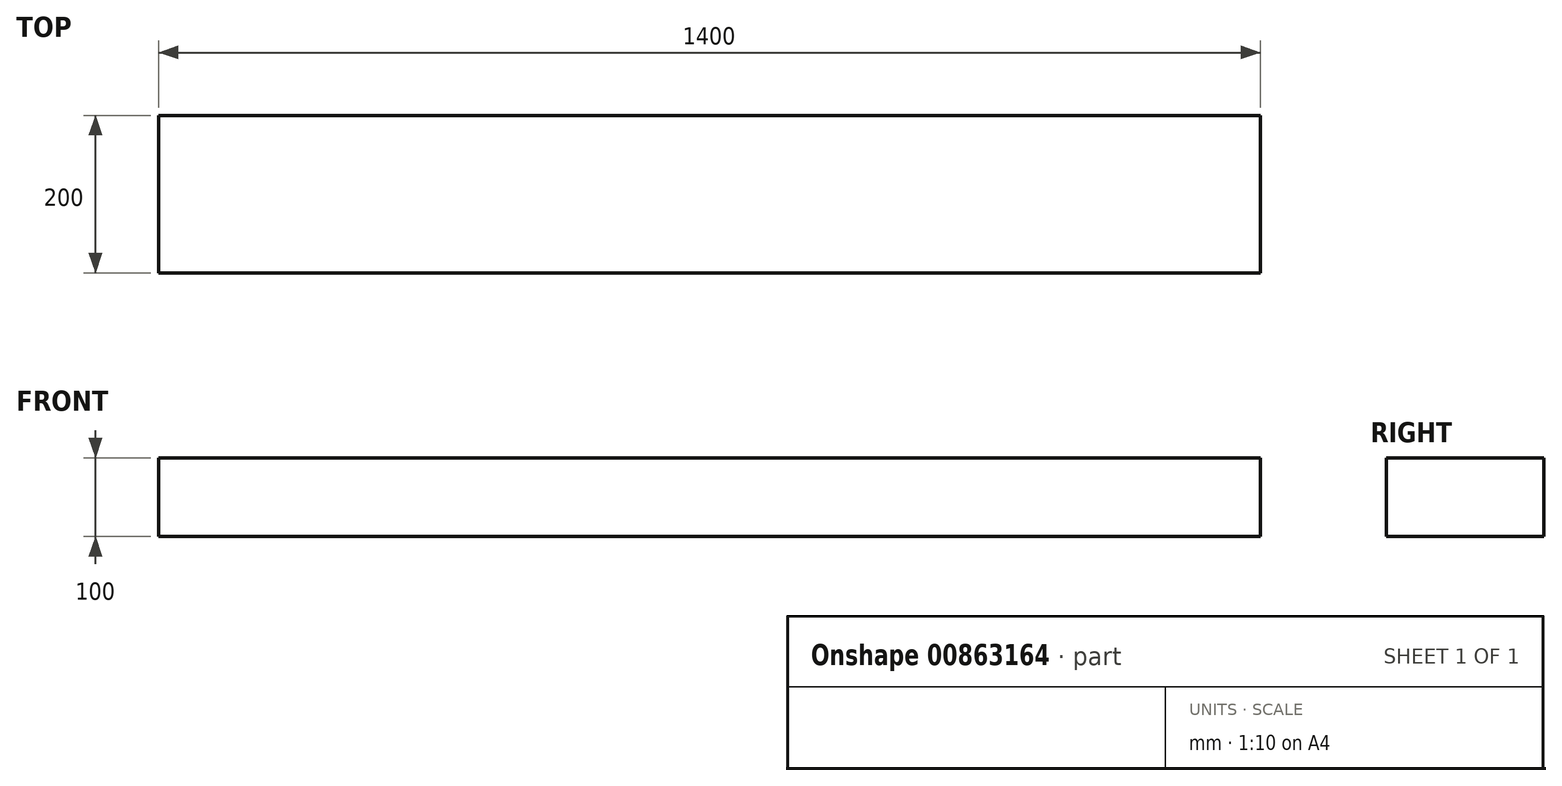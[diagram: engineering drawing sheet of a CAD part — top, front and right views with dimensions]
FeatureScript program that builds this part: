
annotation { "Feature Type Name" : "Feature", "Feature Type Description" : "" }
export const myFeature = defineFeature(function(context is Context, id is Id, definition is map)
    precondition{}
    {
        {
            var Q0;
            Q0=qCreatedBy(makeId("Top.planeOp"),FACE);
            var sketch = newSketch(context, id + "F0", { "sketchPlane" : qUnion([Q0])});
            skLineSegment(sketch, "E0", {"start": v(0, 0) * mm, "end": v(0, 200) * mm});
            skLineSegment(sketch, "E1", {"start": v(0, 200) * mm, "end": v(1400, 200) * mm});
            skLineSegment(sketch, "E2", {"start": v(1400, 200) * mm, "end": v(1400, 0) * mm});
            skLineSegment(sketch, "E3", {"start": v(1400, 0) * mm, "end": v(0, 0) * mm});
            skSolve(sketch);
        }
        {
            var Q0;
            Q0=makeQuery(id+"F0.imprint","IMPRINT",FACE,{"disambiguationData":[TD([[makeQuery(id+"F0.imprint","IMPRINT",EDGE,{"derivedFrom":sQuery(id+"F0.wireOp",EDGE,"E0")}),-1.0]])]});
            extrude(context, id + "F1", {"entities" : qUnion([Q0]), "depth" : 100 * mm, "offsetDistance" : 25 * mm});
        }
    });
